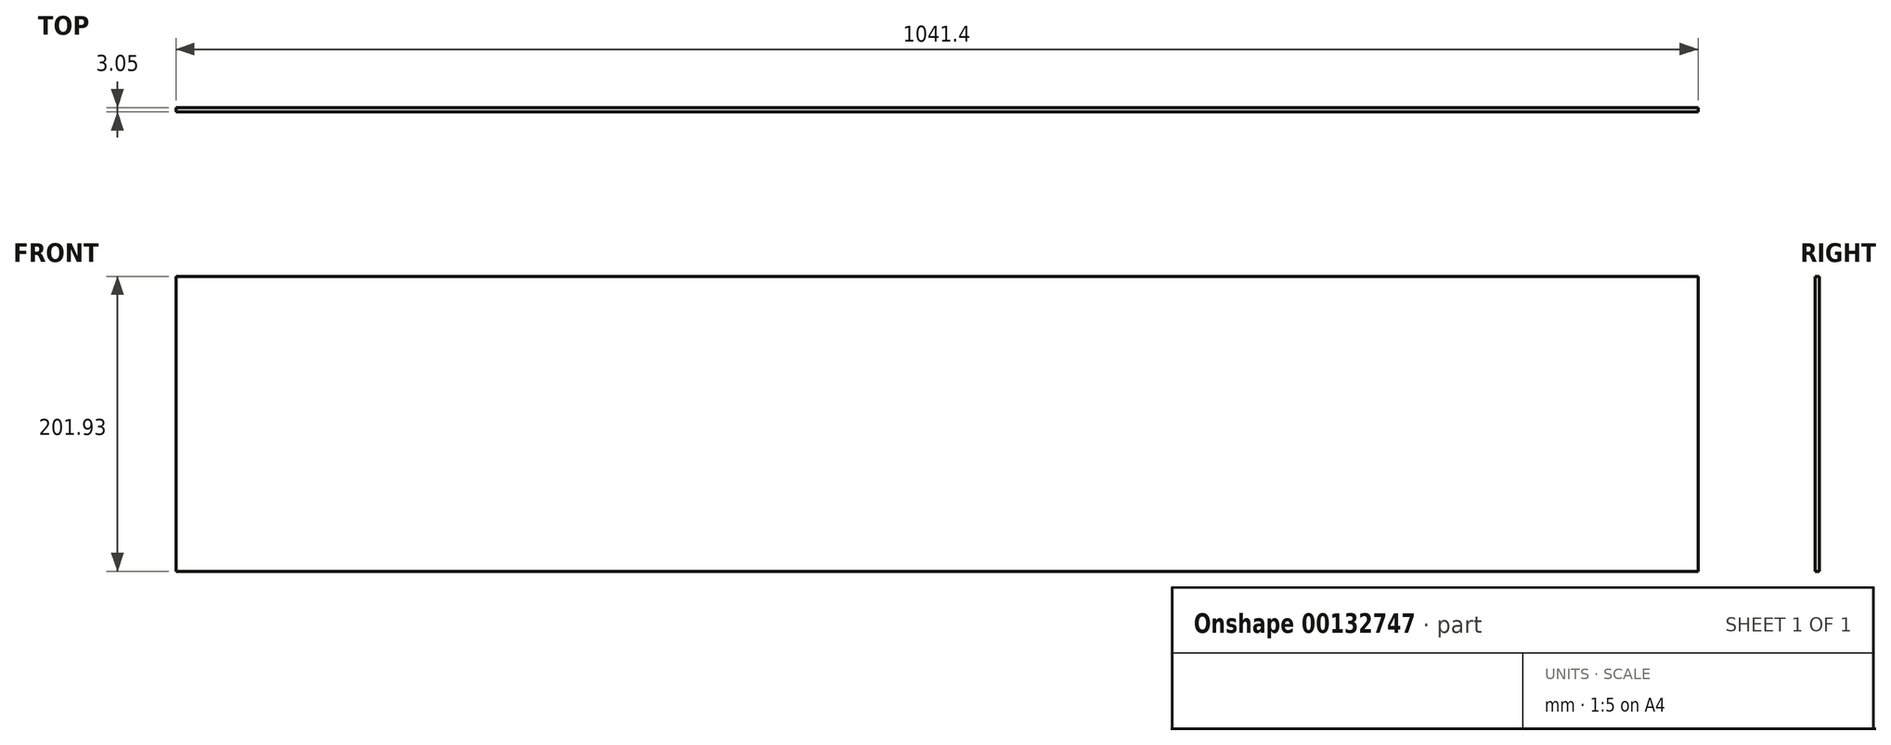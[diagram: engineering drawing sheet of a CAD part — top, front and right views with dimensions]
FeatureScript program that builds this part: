
annotation { "Feature Type Name" : "Feature", "Feature Type Description" : "" }
export const myFeature = defineFeature(function(context is Context, id is Id, definition is map)
    precondition{}
    {
        {
            var Q0;
            Q0=qCreatedBy(makeId("Front.planeOp"),FACE);
            var sketch = newSketch(context, id + "F0", { "sketchPlane" : qUnion([Q0])});
            skLineSegment(sketch, "E0.bottom", {"start": v(-520.7, 201.93) * mm, "end": v(520.7, 201.93) * mm});
            skLineSegment(sketch, "E0.top", {"start": v(-520.7, 0) * mm, "end": v(520.7, 0) * mm});
            skLineSegment(sketch, "E0.left", {"start": v(-520.7, 201.93) * mm, "end": v(-520.7, 0) * mm});
            skLineSegment(sketch, "E0.right", {"start": v(520.7, 201.93) * mm, "end": v(520.7, 0) * mm});
            skSolve(sketch);
        }
        {
            var Q0;
            Q0 = qSketchRegion(id + "F0", true);
            extrude(context, id + "F1", {"entities" : qUnion([Q0]), "depth" : 3.05 * mm});
        }
    });
